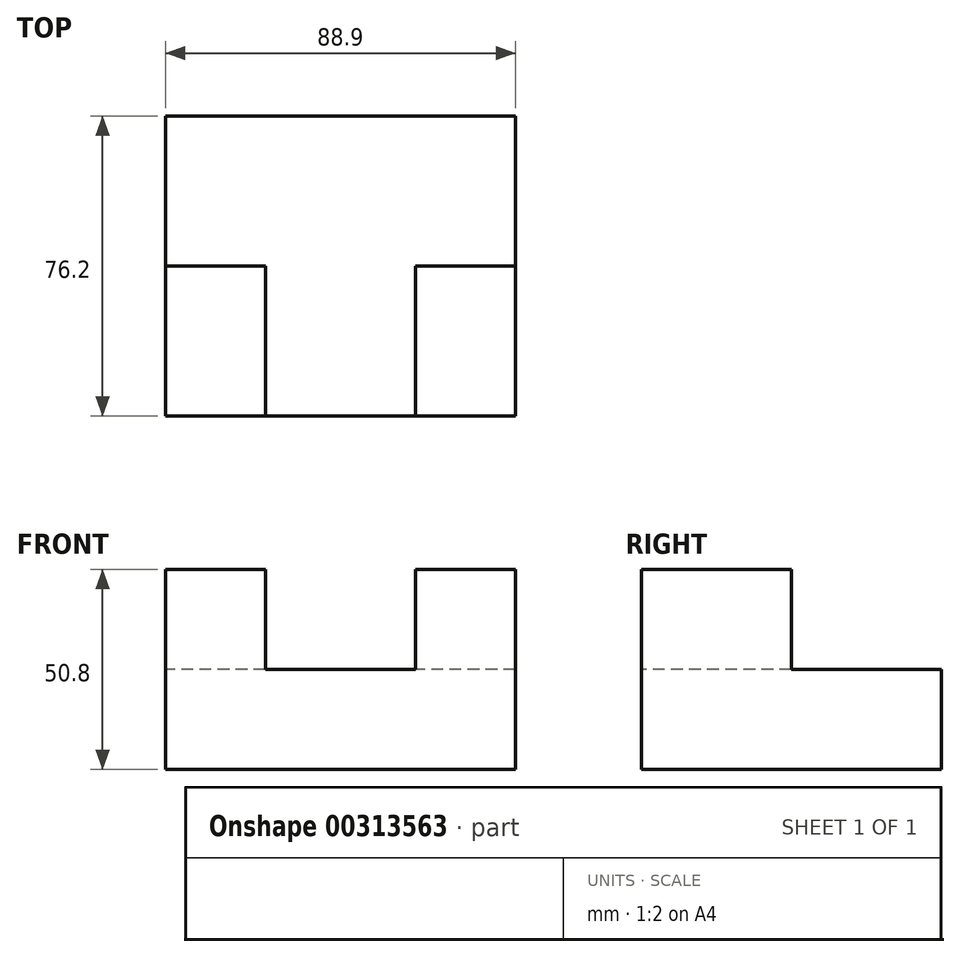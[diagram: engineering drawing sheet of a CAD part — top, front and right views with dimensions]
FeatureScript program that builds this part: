
annotation { "Feature Type Name" : "Feature", "Feature Type Description" : "" }
export const myFeature = defineFeature(function(context is Context, id is Id, definition is map)
    precondition{}
    {
        {
            var Q0;
            Q0=qCreatedBy(makeId("Front.planeOp"),FACE);
            var sketch = newSketch(context, id + "F0", { "sketchPlane" : qUnion([Q0])});
            skLineSegment(sketch, "E0", {"start": v(-44.45, -43.8) * mm, "end": v(44.45, -43.8) * mm});
            skLineSegment(sketch, "E1", {"start": v(44.45, -43.8) * mm, "end": v(44.45, -18.4) * mm});
            skLineSegment(sketch, "E2", {"start": v(44.45, -18.4) * mm, "end": v(-44.45, -18.4) * mm});
            skLineSegment(sketch, "E3", {"start": v(-44.45, -18.4) * mm, "end": v(-44.45, -43.8) * mm});
            skSolve(sketch);
        }
        {
            var Q0;
            Q0 = qSketchRegion(id + "F0", true);
            extrude(context, id + "F1", {"entities" : qUnion([Q0]), "depth" : 76.2 * mm});
        }
        {
            var Q0;
            Q0=makeQuery(id+"F1.opExtrude","CAP_FACE",FACE,{"disambiguationData":[OSD([sQuery(id+"F0.wireOp",EDGE,"E0"),sQuery(id+"F0.wireOp",EDGE,"E1"),sQuery(id+"F0.wireOp",EDGE,"E2"),sQuery(id+"F0.wireOp",EDGE,"E3")])],"isStart":false});
            var sketch = newSketch(context, id + "F2", { "sketchPlane" : qUnion([Q0])});
            skLineSegment(sketch, "E4", {"start": v(44.45, -18.4) * mm, "end": v(44.45, 7) * mm});
            skLineSegment(sketch, "E5", {"start": v(44.45, 7) * mm, "end": v(19.05, 7) * mm});
            skLineSegment(sketch, "E6", {"start": v(19.05, 7) * mm, "end": v(19.05, -18.4) * mm});
            skLineSegment(sketch, "E7", {"start": v(-44.45, -18.4) * mm, "end": v(-44.45, 7) * mm});
            skLineSegment(sketch, "E8", {"start": v(-44.45, 7) * mm, "end": v(-19.05, 7) * mm});
            skLineSegment(sketch, "E9", {"start": v(-19.05, 7) * mm, "end": v(-19.05, -18.4) * mm});
            skSolve(sketch);
        }
        {
            var Q0;
            Q0 = qSketchRegion(id + "F2", true);
            var Q1;
            {var subQ0=sQuery(id+"F2.wireOp",EDGE,"E7");Q1=makeQuery(id+"F2.imprint","IMPRINT",FACE,{"disambiguationData":[TD([[makeQuery(id+"F2.imprint","IMPRINT",EDGE,{"derivedFrom":subQ0}),-1.0]])]});}
            var Q2;
            {var subQ0=sQuery(id+"F2.wireOp",EDGE,"E4");Q2=makeQuery(id+"F2.imprint","IMPRINT",FACE,{"disambiguationData":[TD([[makeQuery(id+"F2.imprint","IMPRINT",EDGE,{"derivedFrom":subQ0}),1.0]])]});}
            extrude(context, id + "F3", {"entities" : qUnion([Q0, Q1, Q2]), "operationType" : NewBodyOperationType.ADD, "depth" : -38.1 * mm});
        }
    });
